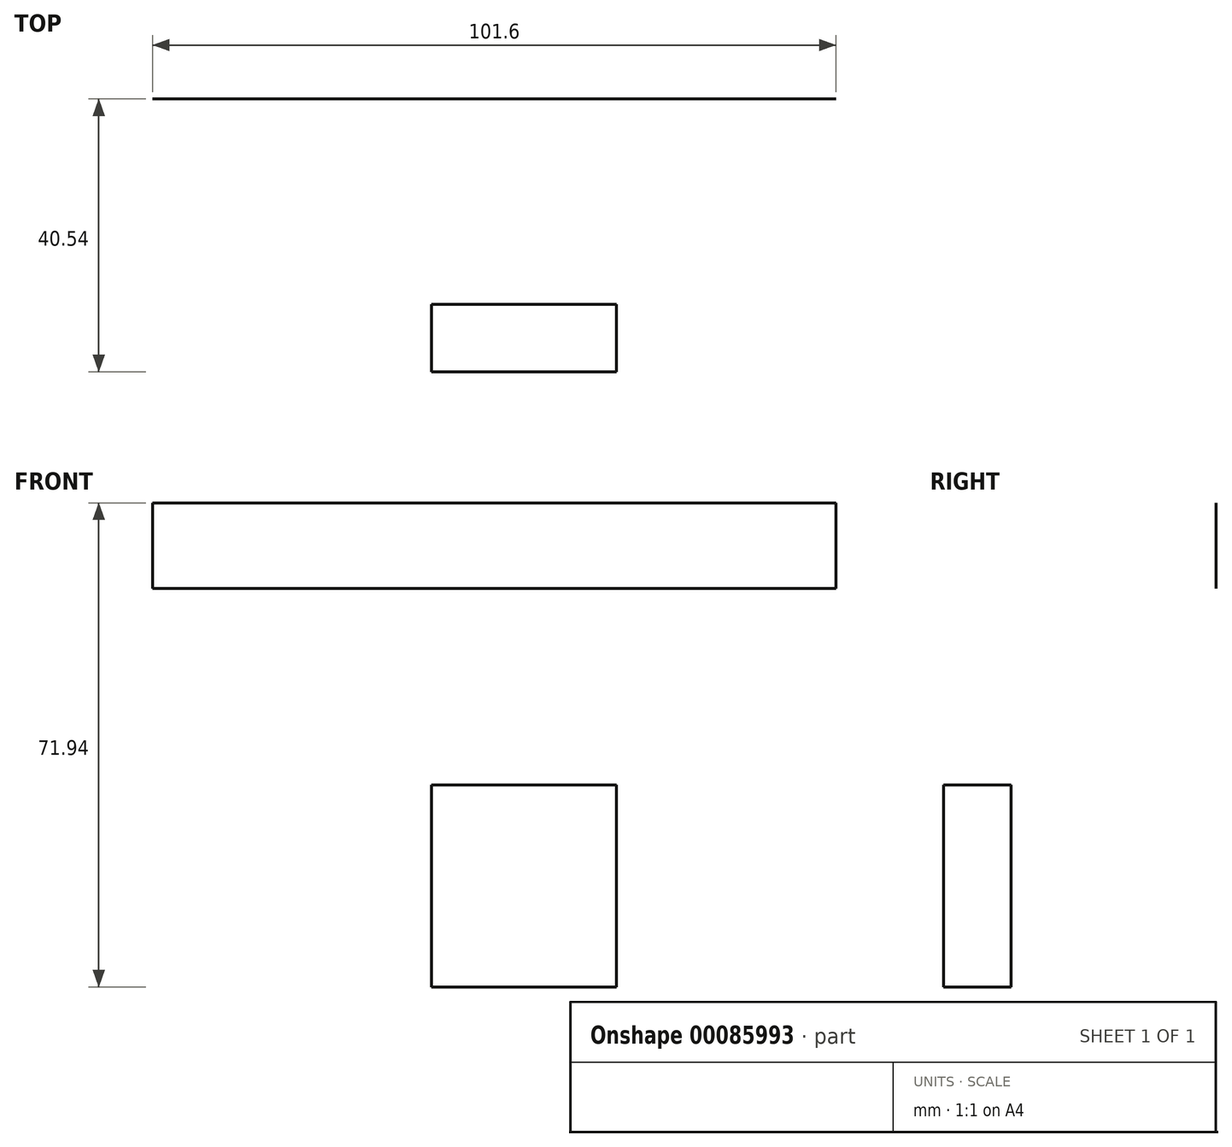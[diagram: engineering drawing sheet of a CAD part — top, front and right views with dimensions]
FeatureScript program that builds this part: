
annotation { "Feature Type Name" : "Feature", "Feature Type Description" : "" }
export const myFeature = defineFeature(function(context is Context, id is Id, definition is map)
    precondition{}
    {
        {
            var Q0;
            Q0=qCreatedBy(makeId("Front.planeOp"),FACE);
            var sketch = newSketch(context, id + "F0", { "sketchPlane" : qUnion([Q0])});
            skLineSegment(sketch, "E0.bottom", {"start": v(-41.47, 0) * mm, "end": v(60.13, 0) * mm});
            skLineSegment(sketch, "E0.top", {"start": v(-41.47, -12.7) * mm, "end": v(60.13, -12.7) * mm});
            skLineSegment(sketch, "E0.left", {"start": v(-41.47, 0) * mm, "end": v(-41.47, -12.7) * mm});
            skLineSegment(sketch, "E0.right", {"start": v(60.13, 0) * mm, "end": v(60.13, -12.7) * mm});
            skSolve(sketch);
        }
        {
            var Q0;
            Q0=makeQuery(id+"F0.imprint","IMPRINT",FACE,{"disambiguationData":[TD([[makeQuery(id+"F0.imprint","IMPRINT",EDGE,{"derivedFrom":sQuery(id+"F0.wireOp",EDGE,"E0.bottom")}),-1.0]])]});
            extrude(context, id + "F1", {"entities" : qUnion([Q0]), "depth" : 1 / 203.2 * mm});
        }
        {
            var Q0;
            Q0=qCreatedBy(makeId("Right.planeOp"),FACE);
            var sketch = newSketch(context, id + "F2", { "sketchPlane" : qUnion([Q0])});
            skLineSegment(sketch, "E1.bottom", {"start": v(-40.54, -71.94) * mm, "end": v(-30.54, -71.94) * mm});
            skLineSegment(sketch, "E1.top", {"start": v(-40.54, -41.94) * mm, "end": v(-30.54, -41.94) * mm});
            skLineSegment(sketch, "E1.left", {"start": v(-40.54, -71.94) * mm, "end": v(-40.54, -41.94) * mm});
            skLineSegment(sketch, "E1.right", {"start": v(-30.54, -71.94) * mm, "end": v(-30.54, -41.94) * mm});
            skSolve(sketch);
        }
        {
            var Q0;
            Q0=makeQuery(id+"F2.imprint","IMPRINT",FACE,{"disambiguationData":[TD([[makeQuery(id+"F2.imprint","IMPRINT",EDGE,{"derivedFrom":sQuery(id+"F2.wireOp",EDGE,"E1.bottom")}),1.0]])]});
            extrude(context, id + "F3", {"entities" : qUnion([Q0]), "depth" : 27.5 * mm});
        }
    });
